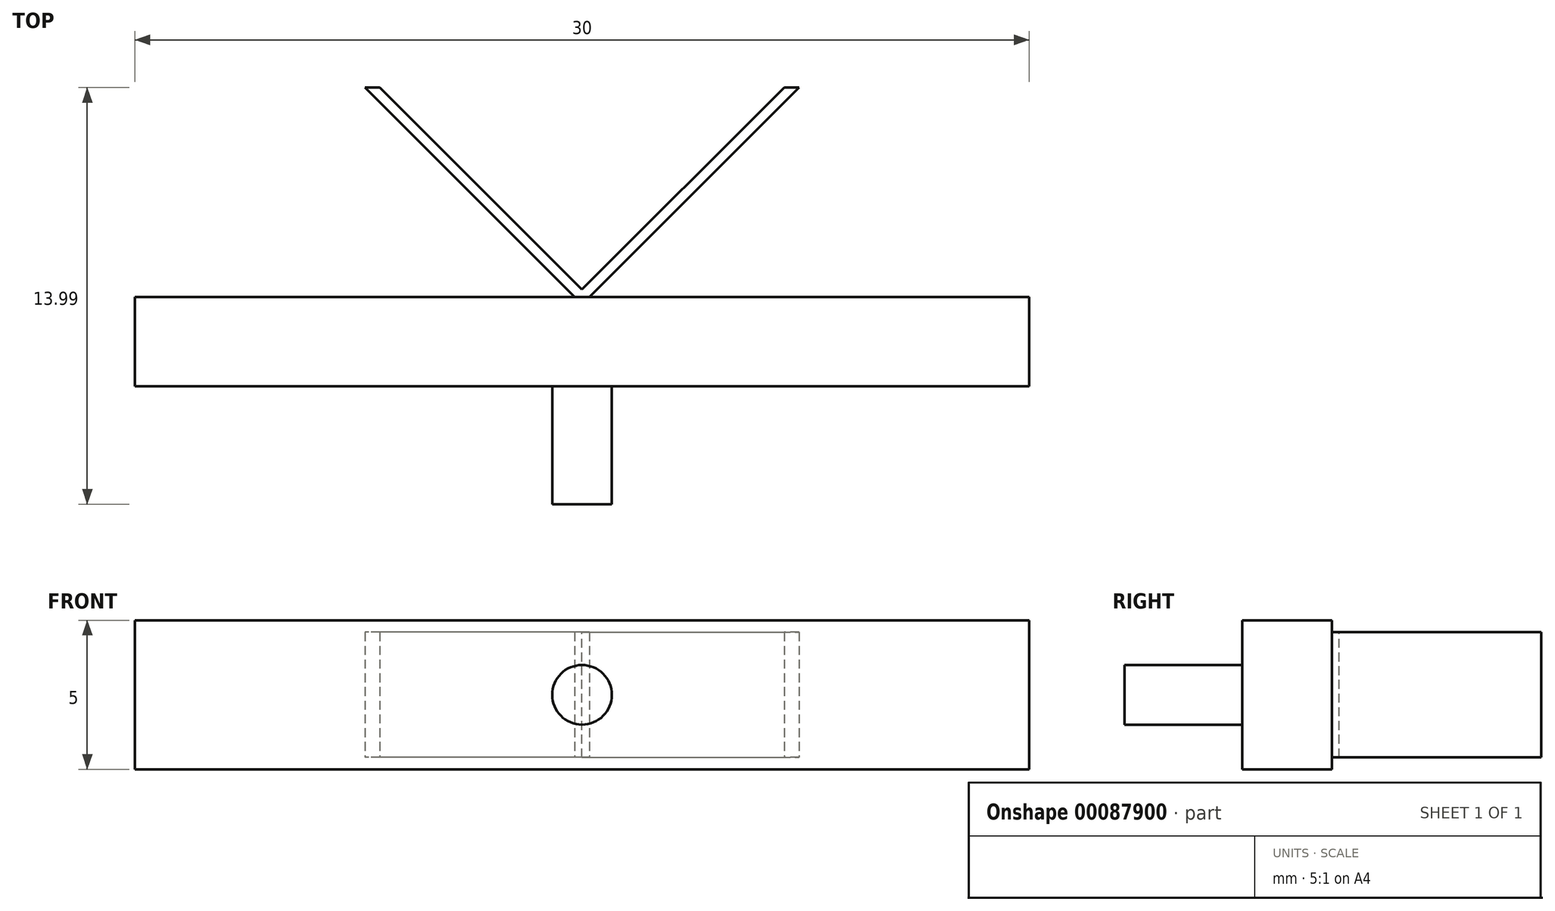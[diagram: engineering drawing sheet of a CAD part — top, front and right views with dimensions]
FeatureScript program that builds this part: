
annotation { "Feature Type Name" : "Feature", "Feature Type Description" : "" }
export const myFeature = defineFeature(function(context is Context, id is Id, definition is map)
    precondition{}
    {
        {
            var Q0;
            Q0=qCreatedBy(makeId("Front.planeOp"),FACE);
            var sketch = newSketch(context, id + "F0", { "sketchPlane" : qUnion([Q0])});
            skLineSegment(sketch, "E0.bottom", {"start": v(15, 2.5) * mm, "end": v(-15, 2.5) * mm});
            skLineSegment(sketch, "E0.top", {"start": v(15, -2.5) * mm, "end": v(-15, -2.5) * mm});
            skLineSegment(sketch, "E0.left", {"start": v(15, 2.5) * mm, "end": v(15, -2.5) * mm});
            skLineSegment(sketch, "E0.right", {"start": v(-15, 2.5) * mm, "end": v(-15, -2.5) * mm});
            skPoint(sketch, "E0.middle", {"position": v(0, 0) * mm});
            skCircle(sketch, "E1", {"center": v(0, 0) * mm, "radius": 1 * mm});
            skSolve(sketch);
        }
        {
            var Q0;
            Q0 = qSketchRegion(id + "F0", true);
            extrude(context, id + "F1", {"entities" : qUnion([Q0]), "depth" : 3 * mm});
        }
        {
            var Q0;
            Q0=makeQuery(id+"F0.imprint","IMPRINT",FACE,{"disambiguationData":[TD([[makeQuery(id+"F0.imprint","IMPRINT",EDGE,{"derivedFrom":sQuery(id+"F0.wireOp",EDGE,"E1")}),1.0]])]});
            extrude(context, id + "F2", {"entities" : qUnion([Q0]), "operationType" : NewBodyOperationType.ADD, "depth" : 6.96 * mm});
        }
        {
            var Q0;
            Q0=qCreatedBy(makeId("Top.planeOp"),FACE);
            var sketch = newSketch(context, id + "F3", { "sketchPlane" : qUnion([Q0])});
            skLineSegment(sketch, "E2", {"start": v(7.04, 7.03) * mm, "end": v(0, 0) * mm});
            skLineSegment(sketch, "E3.MirrorCS", {"start": v(-7.04, 7.03) * mm, "end": v(0, 0) * mm});
            skSolve(sketch);
        }
        {
            var Q0;
            {var subQ0=sQuery(id+"F0.wireOp",EDGE,"E1");Q0=makeQuery(id+"F2.boolean.opBoolean","MERGE",FACE,{"derivedFrom":[makeQuery(id+"F1.opExtrude","CAP_FACE",FACE,{"disambiguationData":[OSD([sQuery(id+"F0.wireOp",EDGE,"E0.bottom"),sQuery(id+"F0.wireOp",EDGE,"E0.top"),sQuery(id+"F0.wireOp",EDGE,"E0.left"),sQuery(id+"F0.wireOp",EDGE,"E0.right"),subQ0])],"isStart":true}),makeQuery(id+"F2.opExtrude","CAP_FACE",FACE,{"disambiguationData":[OSD([subQ0])],"isStart":true})]});}
            var sketch = newSketch(context, id + "F4", { "sketchPlane" : qUnion([Q0])});
            skLineSegment(sketch, "E4.bottom", {"start": v(-0.25, 2.1) * mm, "end": v(0.25, 2.1) * mm});
            skLineSegment(sketch, "E4.top", {"start": v(-0.25, -2.1) * mm, "end": v(0.25, -2.1) * mm});
            skLineSegment(sketch, "E4.left", {"start": v(-0.25, 2.1) * mm, "end": v(-0.25, -2.1) * mm});
            skLineSegment(sketch, "E4.right", {"start": v(0.25, 2.1) * mm, "end": v(0.25, -2.1) * mm});
            skPoint(sketch, "E4.middle", {"position": v(0, 0) * mm});
            skSolve(sketch);
        }
        {
            var Q0;
            Q0 = qSketchRegion(id + "F4", true);
            var Q1;
            Q1=sQuery(id+"F3.wireOp",EDGE,"E3.MirrorCS");
            sweep(context, id + "F5", {"operationType" : NewBodyOperationType.ADD, "profiles" : qUnion([Q0]), "path" : qUnion([Q1])});
        }
        {
            var Q0;
            Q0 = qSketchRegion(id + "F4", true);
            var Q1;
            Q1=sQuery(id+"F3.wireOp",EDGE,"E2");
            sweep(context, id + "F6", {"operationType" : NewBodyOperationType.ADD, "profiles" : qUnion([Q0]), "path" : qUnion([Q1])});
        }
    });
